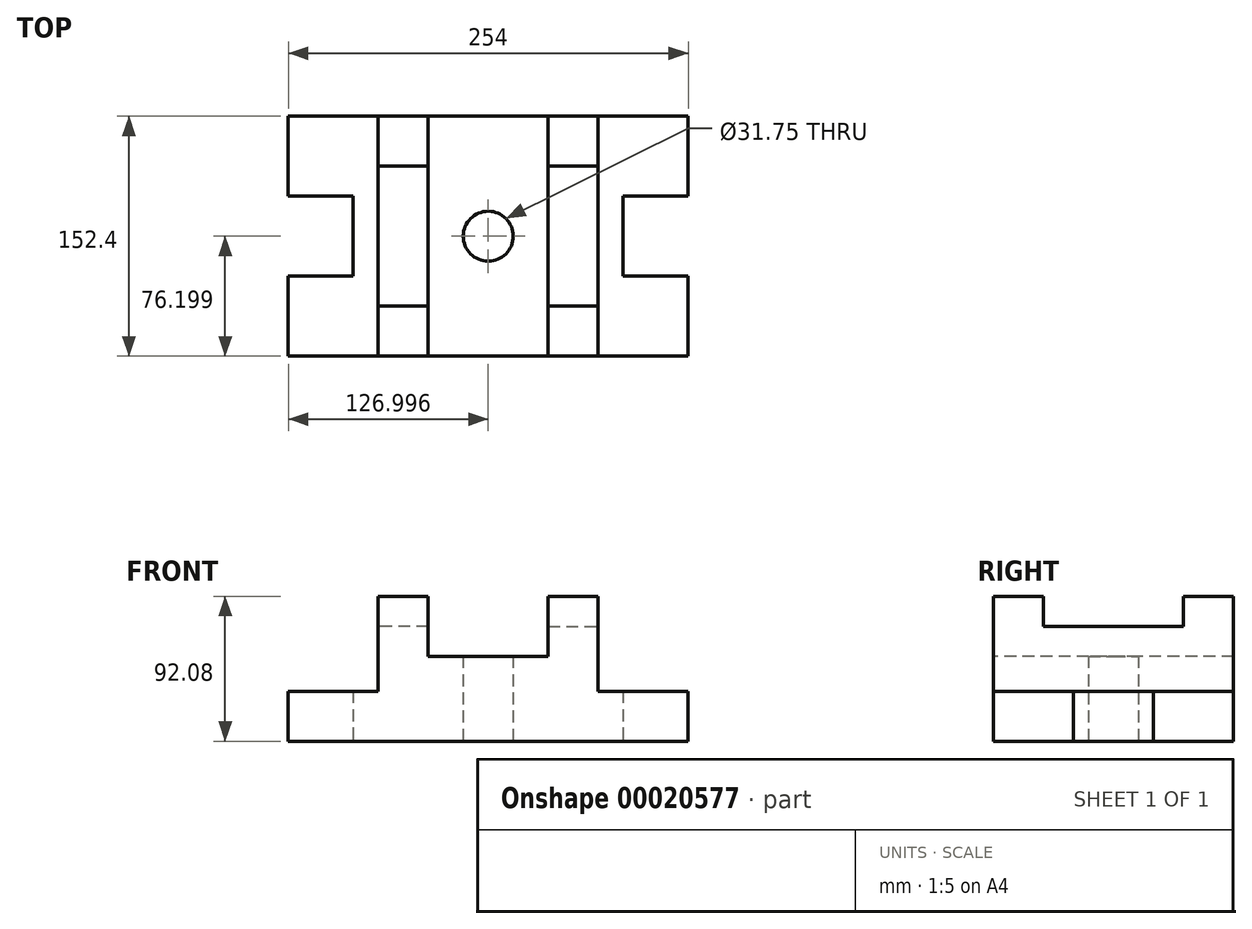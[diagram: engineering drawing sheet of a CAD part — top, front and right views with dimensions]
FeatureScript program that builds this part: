
annotation { "Feature Type Name" : "Feature", "Feature Type Description" : "" }
export const myFeature = defineFeature(function(context is Context, id is Id, definition is map)
    precondition{}
    {
        {
            var Q0;
            Q0=qCreatedBy(makeId("Top.planeOp"),FACE);
            var sketch = newSketch(context, id + "F0", { "sketchPlane" : qUnion([Q0])});
            skLineSegment(sketch, "E0", {"start": v(71.57, -59.37) * mm, "end": v(71.57, -8.57) * mm});
            skLineSegment(sketch, "E1", {"start": v(71.57, -8.57) * mm, "end": v(30.3, -8.57) * mm});
            skLineSegment(sketch, "E2", {"start": v(30.3, -8.57) * mm, "end": v(30.3, 16.83) * mm});
            skLineSegment(sketch, "E3", {"start": v(71.57, -59.37) * mm, "end": v(-55.43, -59.37) * mm});
            skLineSegment(sketch, "E4", {"start": v(-55.43, 16.83) * mm, "end": v(-17.33, 16.83) * mm});
            skLineSegment(sketch, "E5", {"start": v(-17.33, 16.83) * mm, "end": v(-17.33, -59.37) * mm});
            skLineSegment(sketch, "E6", {"start": v(14.42, -24.58) * mm, "end": v(14.42, -59.37) * mm});
            skLineSegment(sketch, "E7", {"start": v(-17.33, 16.83) * mm, "end": v(30.3, 16.83) * mm});
            skLineSegment(sketch, "E8", {"start": v(14.42, -24.58) * mm, "end": v(14.42, 16.83) * mm});
            skLineSegment(sketch, "E9", {"start": v(-17.33, -27.62) * mm, "end": v(14.42, -27.62) * mm});
            skArc(sketch, "E10", {"start": v(-55.58, 8.9) * mm, "mid": v(-55.5, 8.9) * mm, "end": v(-55.43, 8.9) * mm});
            skArc(sketch, "E11", {"start": v(-55.43, 0.95) * mm, "mid": v(-44.2, 5.6) * mm, "end": v(-39.56, 16.83) * mm});
            skLineSegment(sketch, "E12", {"start": v(-55.43, -59.37) * mm, "end": v(-55.43, 16.83) * mm});
            skSolve(sketch);
        }
        {
            var Q0;
            {var subQ7=sQuery(id+"F0.wireOp",EDGE,"E0");Q0=makeQuery(id+"F0.imprint","IMPRINT",FACE,{"disambiguationData":[TD([[makeQuery(id+"F0.imprint","IMPRINT",EDGE,{"derivedFrom":subQ7}),1.0]])]});}
            extrude(context, id + "F1", {"entities" : qUnion([Q0]), "depth" : 31.75 * mm});
        }
        {
            var Q0;
            {var subQ0=sQuery(id+"F0.wireOp",EDGE,"E9");Q0=makeQuery(id+"F0.imprint","IMPRINT",FACE,{"disambiguationData":[TD([[makeQuery(id+"F0.imprint","IMPRINT",EDGE,{"derivedFrom":subQ0}),-1.0]])]});}
            extrude(context, id + "F2", {"entities" : qUnion([Q0]), "operationType" : NewBodyOperationType.ADD, "depth" : 92.07 * mm});
        }
        {
            var Q0;
            {var subQ0=sQuery(id+"F0.wireOp",EDGE,"E8");Q0=makeQuery(id+"F0.imprint","IMPRINT",FACE,{"disambiguationData":[TD([[makeQuery(id+"F0.imprint","IMPRINT",EDGE,{"derivedFrom":subQ0}),1.0]])]});}
            extrude(context, id + "F3", {"entities" : qUnion([Q0]), "operationType" : NewBodyOperationType.ADD, "depth" : 73.02 * mm});
        }
        {
            var Q0;
            {var subQ1=sQuery(id+"F0.wireOp",EDGE,"fffc2a7a-0f66-4457-99d8-cd5d7c254d0c");var subQ7=sQuery(id+"F0.wireOp",EDGE,"E3");var subQ10=makeQuery(id+"F0.imprint","INTERSECT",VERTEX,{"derivedFrom":[subQ7,subQ1]});Q0=makeQuery(id+"F0.imprint","IMPRINT",FACE,{"disambiguationData":[TD([[makeQuery(id+"F0.imprint","IMPRINT",EDGE,{"disambiguationData":[TD([[subQ10,1.0]])],"derivedFrom":subQ7}),-1.0]])]});}
            extrude(context, id + "F4", {"entities" : qUnion([Q0]), "depth" : 53.97 * mm});
        }
        {
            var Q0;
            Q0=makeQuery(id+"F4.opExtrude","SWEPT_BODY",BODY,{"disambiguationData":[OSD([sQuery(id+"F0.wireOp",EDGE,"E3"),sQuery(id+"F0.wireOp",EDGE,"fffc2a7a-0f66-4457-99d8-cd5d7c254d0c"),sQuery(id+"F0.wireOp",EDGE,"E4"),sQuery(id+"F0.wireOp",EDGE,"E5"),sQuery(id+"F0.wireOp",EDGE,"E10")])]});
            deleteBodies(context, id + "F5", {"entities" : qUnion([Q0])});
        }
        {
            var Q0;
            {var subQ1=sQuery(id+"F0.wireOp",EDGE,"fffc2a7a-0f66-4457-99d8-cd5d7c254d0c");var subQ7=sQuery(id+"F0.wireOp",EDGE,"E3");var subQ10=makeQuery(id+"F0.imprint","INTERSECT",VERTEX,{"derivedFrom":[subQ7,subQ1]});Q0=makeQuery(id+"F0.imprint","IMPRINT",FACE,{"disambiguationData":[TD([[makeQuery(id+"F0.imprint","IMPRINT",EDGE,{"disambiguationData":[TD([[subQ10,1.0]])],"derivedFrom":subQ7}),-1.0]])]});}
            extrude(context, id + "F6", {"entities" : qUnion([Q0]), "operationType" : NewBodyOperationType.ADD, "depth" : 53.97 * mm});
        }
        {
            var Q0;
            {var subQ1=sQuery(id+"F0.wireOp",EDGE,"E11");Q0=makeQuery(id+"F0.imprint","IMPRINT",FACE,{"disambiguationData":[TD([[makeQuery(id+"F0.imprint","IMPRINT",EDGE,{"derivedFrom":subQ1}),-1.0]])]});}
            extrude(context, id + "F7", {"entities" : qUnion([Q0]), "operationType" : NewBodyOperationType.ADD, "depth" : 53.97 * mm});
        }
        {
            var Q0;
            Q0=makeQuery(id+"F1.opExtrude","SWEPT_BODY",BODY,{"disambiguationData":[OSD([sQuery(id+"F0.wireOp",EDGE,"E0"),sQuery(id+"F0.wireOp",EDGE,"E1"),sQuery(id+"F0.wireOp",EDGE,"E2"),sQuery(id+"F0.wireOp",EDGE,"E3"),sQuery(id+"F0.wireOp",EDGE,"E6"),sQuery(id+"F0.wireOp",EDGE,"E7"),sQuery(id+"F0.wireOp",EDGE,"E8")])]});
            var Q1;
            Q1=makeQuery(id+"F7.opExtrude","SWEPT_FACE",FACE,{"disambiguationData":[OSD([sQuery(id+"F0.wireOp",EDGE,"E12")])]});
            mirror(context, id + "F8", {"operationType" : NewBodyOperationType.ADD, "entities" : qUnion([Q0]), "mirrorPlane" : qUnion([Q1])});
        }
        {
            var Q0;
            Q0=makeQuery(id+"F1.opExtrude","SWEPT_BODY",BODY,{"disambiguationData":[OSD([sQuery(id+"F0.wireOp",EDGE,"E0"),sQuery(id+"F0.wireOp",EDGE,"E1"),sQuery(id+"F0.wireOp",EDGE,"E2"),sQuery(id+"F0.wireOp",EDGE,"E3"),sQuery(id+"F0.wireOp",EDGE,"E6"),sQuery(id+"F0.wireOp",EDGE,"E7"),sQuery(id+"F0.wireOp",EDGE,"E8")])]});
            var Q1;
            {var subQ0=sQuery(id+"F0.wireOp",EDGE,"E7");Q1=makeQuery(id+"F7.boolean.opBoolean","MERGE",FACE,{"derivedFrom":[makeQuery(id+"F3.boolean.opBoolean","MERGE",FACE,{"derivedFrom":[makeQuery(id+"F1.opExtrude","SWEPT_FACE",FACE,{"disambiguationData":[OSD([subQ0])]}),makeQuery(id+"F3.opExtrude","SWEPT_FACE",FACE,{"disambiguationData":[OSD([subQ0])]})]}),makeQuery(id+"F7.opExtrude","SWEPT_FACE",FACE,{"disambiguationData":[OSD([sQuery(id+"F0.wireOp",EDGE,"E4")])]})]});}
            mirror(context, id + "F9", {"operationType" : NewBodyOperationType.ADD, "entities" : qUnion([Q0]), "mirrorPlane" : qUnion([Q1])});
        }
    });
